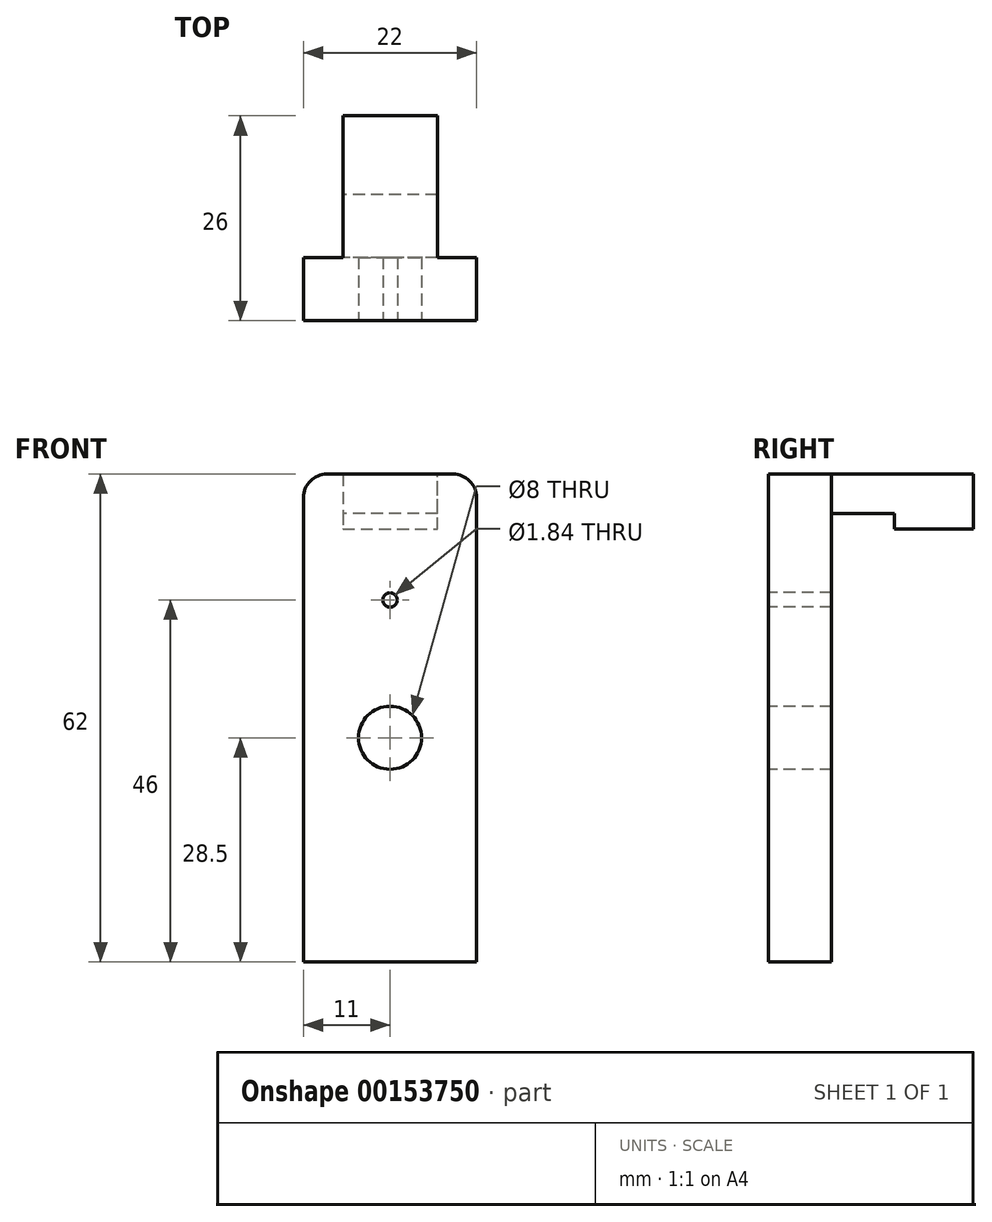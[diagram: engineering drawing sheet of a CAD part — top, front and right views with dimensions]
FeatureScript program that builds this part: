
annotation { "Feature Type Name" : "Feature", "Feature Type Description" : "" }
export const myFeature = defineFeature(function(context is Context, id is Id, definition is map)
    precondition{}
    {
        {
            var Q0;
            Q0=qCreatedBy(makeId("Front.planeOp"),FACE);
            var sketch = newSketch(context, id + "F0", { "sketchPlane" : qUnion([Q0])});
            skLineSegment(sketch, "E0.left", {"start": v(11, 17.5) * mm, "end": v(11, -17.5) * mm});
            skLineSegment(sketch, "E0.right", {"start": v(-11, 17.5) * mm, "end": v(-11, -17.5) * mm});
            skPoint(sketch, "E0.middle", {"position": v(0, 0) * mm});
            skCircle(sketch, "E1", {"center": v(0, 0) * mm, "radius": 4 * mm});
            skCircle(sketch, "E2", {"center": v(0, 17.5) * mm, "radius": 0.92 * mm});
            skPoint(sketch, "E3.orphan", {"position": v(11, 30) * mm});
            skPoint(sketch, "E4.orphan", {"position": v(11, -27.63) * mm});
            skPoint(sketch, "E5.orphan", {"position": v(-11, -30) * mm});
            skLineSegment(sketch, "E6", {"start": v(0, 33.5) * mm, "end": v(8, 33.5) * mm});
            skLineSegment(sketch, "E7", {"start": v(-11, 17.5) * mm, "end": v(-11, 28.5) * mm});
            skLineSegment(sketch, "E8", {"start": v(0, 33.5) * mm, "end": v(-6, 33.5) * mm});
            skLineSegment(sketch, "E9", {"start": v(11, 17.5) * mm, "end": v(11, 30.5) * mm});
            skPoint(sketch, "E10.visualSharp", {"position": v(-11, 33.5) * mm});
            skPoint(sketch, "E11.visualSharp", {"position": v(11, 33.5) * mm});
            skArc(sketch, "E11.filletArc", {"start": v(11, 30.5) * mm, "mid": v(10.12, 32.62) * mm, "end": v(8, 33.5) * mm});
            skLineSegment(sketch, "E12", {"start": v(-11, 28.5) * mm, "end": v(-11, 30.5) * mm});
            skLineSegment(sketch, "E13", {"start": v(-6, 33.5) * mm, "end": v(-8, 33.5) * mm});
            skArc(sketch, "E14.filletArc", {"start": v(-8, 33.5) * mm, "mid": v(-10.12, 32.62) * mm, "end": v(-11, 30.5) * mm});
            skLineSegment(sketch, "E15", {"start": v(0, 17.5) * mm, "end": v(0, 18.42) * mm});
            skLineSegment(sketch, "E16", {"start": v(0, 28.5) * mm, "end": v(-6, 28.5) * mm});
            skLineSegment(sketch, "E17", {"start": v(0, 28.5) * mm, "end": v(6, 28.5) * mm});
            skLineSegment(sketch, "E18", {"start": v(-6, 26.5) * mm, "end": v(6, 26.5) * mm});
            skLineSegment(sketch, "E19", {"start": v(-6, 33.5) * mm, "end": v(-6, 28.5) * mm});
            skLineSegment(sketch, "E20", {"start": v(6, 26.5) * mm, "end": v(6, 33.5) * mm});
            skLineSegment(sketch, "E21", {"start": v(-6, 28.5) * mm, "end": v(-6, 26.5) * mm});
            skPoint(sketch, "E21.endSnap0", {"position": v(0, 26.5) * mm});
            skPoint(sketch, "E22.orphan", {"position": v(-11, 26.5) * mm});
            skPoint(sketch, "E23.orphan", {"position": v(11, 26.5) * mm});
            skLineSegment(sketch, "E24", {"start": v(-11, -17.5) * mm, "end": v(-11, -28.5) * mm});
            skLineSegment(sketch, "E25", {"start": v(11, -17.5) * mm, "end": v(11, -28.5) * mm});
            skLineSegment(sketch, "E26", {"start": v(0, -28.5) * mm, "end": v(11, -28.5) * mm});
            skLineSegment(sketch, "E27", {"start": v(0, -28.5) * mm, "end": v(-11, -28.5) * mm});
            skPoint(sketch, "E28.center.orphan", {"position": v(0, -17.5) * mm});
            skSolve(sketch);
        }
        {
            var Q0;
            Q0=makeQuery(id+"F0.imprint","IMPRINT",FACE,{"disambiguationData":[TD([[makeQuery(id+"F0.imprint","IMPRINT",EDGE,{"derivedFrom":sQuery(id+"F0.wireOp",EDGE,"E0.left")}),-1.0]])]});
            var Q1;
            {var subQ0=sQuery(id+"F0.wireOp",EDGE,"E16");Q1=makeQuery(id+"F0.imprint","IMPRINT",FACE,{"disambiguationData":[TD([[makeQuery(id+"F0.imprint","IMPRINT",EDGE,{"derivedFrom":subQ0}),1.0]])]});}
            var Q2;
            {var subQ0=sQuery(id+"F0.wireOp",EDGE,"E17");Q2=makeQuery(id+"F0.imprint","IMPRINT",FACE,{"disambiguationData":[TD([[makeQuery(id+"F0.imprint","IMPRINT",EDGE,{"derivedFrom":subQ0}),-1.0]])]});}
            var Q3;
            {var subQ1=sQuery(id+"F0.wireOp",EDGE,"E8");Q3=makeQuery(id+"F0.imprint","IMPRINT",FACE,{"disambiguationData":[TD([[makeQuery(id+"F0.imprint","IMPRINT",EDGE,{"derivedFrom":subQ1}),1.0]])]});}
            extrude(context, id + "F1", {"entities" : qUnion([Q0, Q1, Q2, Q3]), "oppositeDirection" : true, "depth" : 8 * mm});
        }
        {
            var Q0;
            {var subQ1=sQuery(id+"F0.wireOp",EDGE,"E8");Q0=makeQuery(id+"F0.imprint","IMPRINT",FACE,{"disambiguationData":[TD([[makeQuery(id+"F0.imprint","IMPRINT",EDGE,{"derivedFrom":subQ1}),1.0]])]});}
            extrude(context, id + "F2", {"entities" : qUnion([Q0]), "operationType" : NewBodyOperationType.ADD, "oppositeDirection" : true, "depth" : 16 * mm});
        }
        {
            var Q0;
            {var subQ1=sQuery(id+"F0.wireOp",EDGE,"E8");Q0=makeQuery(id+"F0.imprint","IMPRINT",FACE,{"disambiguationData":[TD([[makeQuery(id+"F0.imprint","IMPRINT",EDGE,{"derivedFrom":subQ1}),1.0]])]});}
            var Q1;
            {var subQ0=sQuery(id+"F0.wireOp",EDGE,"E16");Q1=makeQuery(id+"F0.imprint","IMPRINT",FACE,{"disambiguationData":[TD([[makeQuery(id+"F0.imprint","IMPRINT",EDGE,{"derivedFrom":subQ0}),1.0]])]});}
            var Q2;
            {var subQ0=sQuery(id+"F0.wireOp",EDGE,"E17");Q2=makeQuery(id+"F0.imprint","IMPRINT",FACE,{"disambiguationData":[TD([[makeQuery(id+"F0.imprint","IMPRINT",EDGE,{"derivedFrom":subQ0}),-1.0]])]});}
            extrude(context, id + "F3", {"entities" : qUnion([Q0, Q1, Q2]), "operationType" : NewBodyOperationType.ADD, "oppositeDirection" : true, "depth" : 26 * mm, "hasSecondDirection" : true, "secondDirectionOppositeDirection" : true, "secondDirectionDepth" : 16 * mm});
        }
    });
